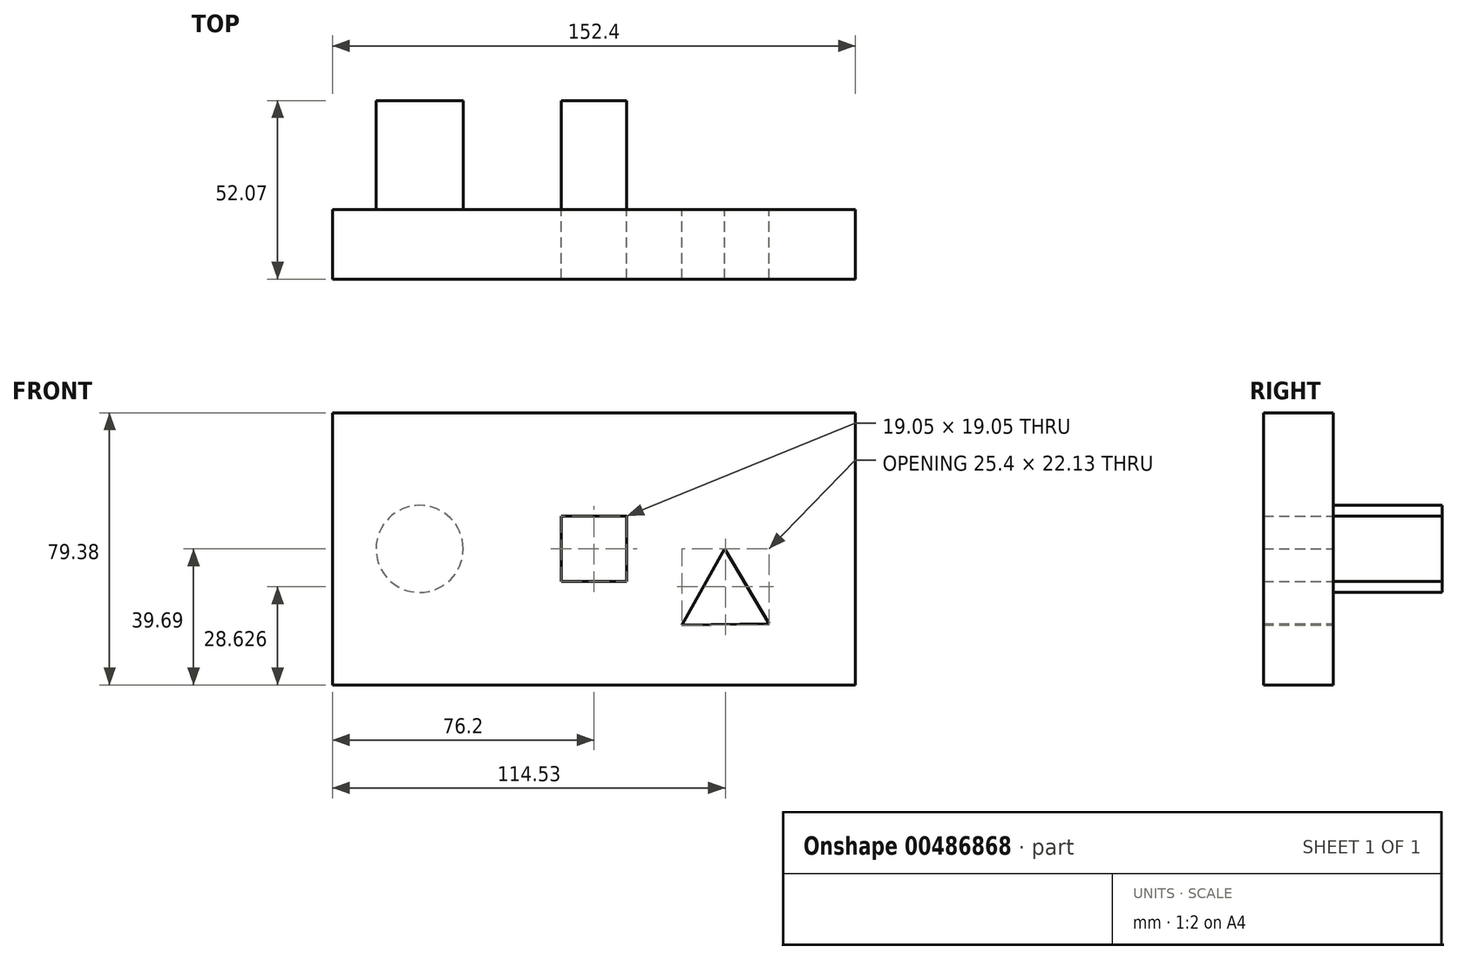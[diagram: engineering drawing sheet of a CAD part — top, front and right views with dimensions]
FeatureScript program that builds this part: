
annotation { "Feature Type Name" : "Feature", "Feature Type Description" : "" }
export const myFeature = defineFeature(function(context is Context, id is Id, definition is map)
    precondition{}
    {
        {
            var Q0;
            Q0=qCreatedBy(makeId("Front.planeOp"),FACE);
            var sketch = newSketch(context, id + "F0", { "sketchPlane" : qUnion([Q0])});
            skLineSegment(sketch, "E0", {"start": v(0, 0) * mm, "end": v(6.35, 0) * mm});
            skLineSegment(sketch, "E1", {"start": v(6.35, 0) * mm, "end": v(-6.12, -22.13) * mm});
            skLineSegment(sketch, "E2", {"start": v(6.35, 0) * mm, "end": v(19.28, -21.86) * mm});
            skLineSegment(sketch, "E3", {"start": v(-6.12, -22.13) * mm, "end": v(19.28, -21.86) * mm});
            skLineSegment(sketch, "E4", {"start": v(0, 0) * mm, "end": v(-31.75, 0) * mm});
            skLineSegment(sketch, "E5.bottom", {"start": v(-22.22, 9.52) * mm, "end": v(-41.28, 9.53) * mm});
            skLineSegment(sketch, "E5.top", {"start": v(-22.23, -9.53) * mm, "end": v(-41.28, -9.52) * mm});
            skLineSegment(sketch, "E5.left", {"start": v(-22.22, 9.52) * mm, "end": v(-22.23, -9.53) * mm});
            skLineSegment(sketch, "E5.right", {"start": v(-41.27, 9.53) * mm, "end": v(-41.28, -9.52) * mm});
            skPoint(sketch, "E5.middle", {"position": v(-31.75, 0) * mm});
            skLineSegment(sketch, "E6", {"start": v(-31.75, 0) * mm, "end": v(-82.55, 0) * mm});
            skCircle(sketch, "E7", {"center": v(-82.55, 0) * mm, "radius": 12.7 * mm});
            skLineSegment(sketch, "E8.bottom", {"start": v(44.45, 39.69) * mm, "end": v(-107.95, 39.69) * mm});
            skLineSegment(sketch, "E8.top", {"start": v(44.45, -39.69) * mm, "end": v(-107.95, -39.69) * mm});
            skLineSegment(sketch, "E8.left", {"start": v(44.45, 39.69) * mm, "end": v(44.45, -39.69) * mm});
            skLineSegment(sketch, "E8.right", {"start": v(-107.95, 39.69) * mm, "end": v(-107.95, -39.69) * mm});
            skSolve(sketch);
        }
        {
            var Q0;
            Q0=makeQuery(id+"F0.imprint","IMPRINT",FACE,{"disambiguationData":[TD([[makeQuery(id+"F0.imprint","IMPRINT",EDGE,{"derivedFrom":sQuery(id+"F0.wireOp",EDGE,"E1")}),-1.0]])]});
            var Q1;
            Q1=makeQuery(id+"F0.imprint","IMPRINT",FACE,{"disambiguationData":[TD([[makeQuery(id+"F0.imprint","IMPRINT",EDGE,{"derivedFrom":sQuery(id+"F0.wireOp",EDGE,"E7")}),1.0]])]});
            var Q2;
            {var subQ1=sQuery(id+"F0.wireOp",EDGE,"E5.top");Q2=makeQuery(id+"F0.imprint","IMPRINT",FACE,{"disambiguationData":[TD([[makeQuery(id+"F0.imprint","IMPRINT",EDGE,{"derivedFrom":subQ1}),-1.0]])]});}
            var Q3;
            {var subQ1=sQuery(id+"F0.wireOp",EDGE,"E5.bottom");Q3=makeQuery(id+"F0.imprint","IMPRINT",FACE,{"disambiguationData":[TD([[makeQuery(id+"F0.imprint","IMPRINT",EDGE,{"derivedFrom":subQ1}),1.0]])]});}
            var Q4;
            Q4=makeQuery(id+"F0.imprint","IMPRINT",FACE,{"disambiguationData":[TD([[makeQuery(id+"F0.imprint","IMPRINT",EDGE,{"derivedFrom":sQuery(id+"F0.wireOp",EDGE,"E1")}),1.0]])]});
            extrude(context, id + "F1", {"entities" : qUnion([Q0, Q1, Q2, Q3, Q4]), "depth" : 20.32 * mm});
        }
        {
            var Q0;
            Q0=makeQuery(id+"F0.imprint","IMPRINT",FACE,{"disambiguationData":[TD([[makeQuery(id+"F0.imprint","IMPRINT",EDGE,{"derivedFrom":sQuery(id+"F0.wireOp",EDGE,"E7")}),1.0]])]});
            extrude(context, id + "F2", {"entities" : qUnion([Q0]), "operationType" : NewBodyOperationType.ADD, "oppositeDirection" : true, "depth" : 31.75 * mm});
        }
        {
            var Q0;
            Q0=makeQuery(id+"F0.imprint","IMPRINT",FACE,{"disambiguationData":[TD([[makeQuery(id+"F0.imprint","IMPRINT",EDGE,{"derivedFrom":sQuery(id+"F0.wireOp",EDGE,"E1")}),1.0]])]});
            extrude(context, id + "F3", {"entities" : qUnion([Q0]), "operationType" : NewBodyOperationType.REMOVE, "depth" : 45.97 * mm});
        }
        {
            var Q0;
            {var subQ1=sQuery(id+"F0.wireOp",EDGE,"E5.top");Q0=makeQuery(id+"F0.imprint","IMPRINT",FACE,{"disambiguationData":[TD([[makeQuery(id+"F0.imprint","IMPRINT",EDGE,{"derivedFrom":subQ1}),-1.0]])]});}
            var Q1;
            {var subQ1=sQuery(id+"F0.wireOp",EDGE,"E5.bottom");Q1=makeQuery(id+"F0.imprint","IMPRINT",FACE,{"disambiguationData":[TD([[makeQuery(id+"F0.imprint","IMPRINT",EDGE,{"derivedFrom":subQ1}),1.0]])]});}
            extrude(context, id + "F4", {"entities" : qUnion([Q0, Q1]), "operationType" : NewBodyOperationType.REMOVE, "depth" : 84.58 * mm});
        }
        {
            var Q0;
            {var subQ1=sQuery(id+"F0.wireOp",EDGE,"E5.top");Q0=makeQuery(id+"F0.imprint","IMPRINT",FACE,{"disambiguationData":[TD([[makeQuery(id+"F0.imprint","IMPRINT",EDGE,{"derivedFrom":subQ1}),-1.0]])]});}
            var Q1;
            {var subQ1=sQuery(id+"F0.wireOp",EDGE,"E5.bottom");Q1=makeQuery(id+"F0.imprint","IMPRINT",FACE,{"disambiguationData":[TD([[makeQuery(id+"F0.imprint","IMPRINT",EDGE,{"derivedFrom":subQ1}),1.0]])]});}
            extrude(context, id + "F5", {"entities" : qUnion([Q0, Q1]), "oppositeDirection" : true, "depth" : 31.75 * mm});
        }
    });
